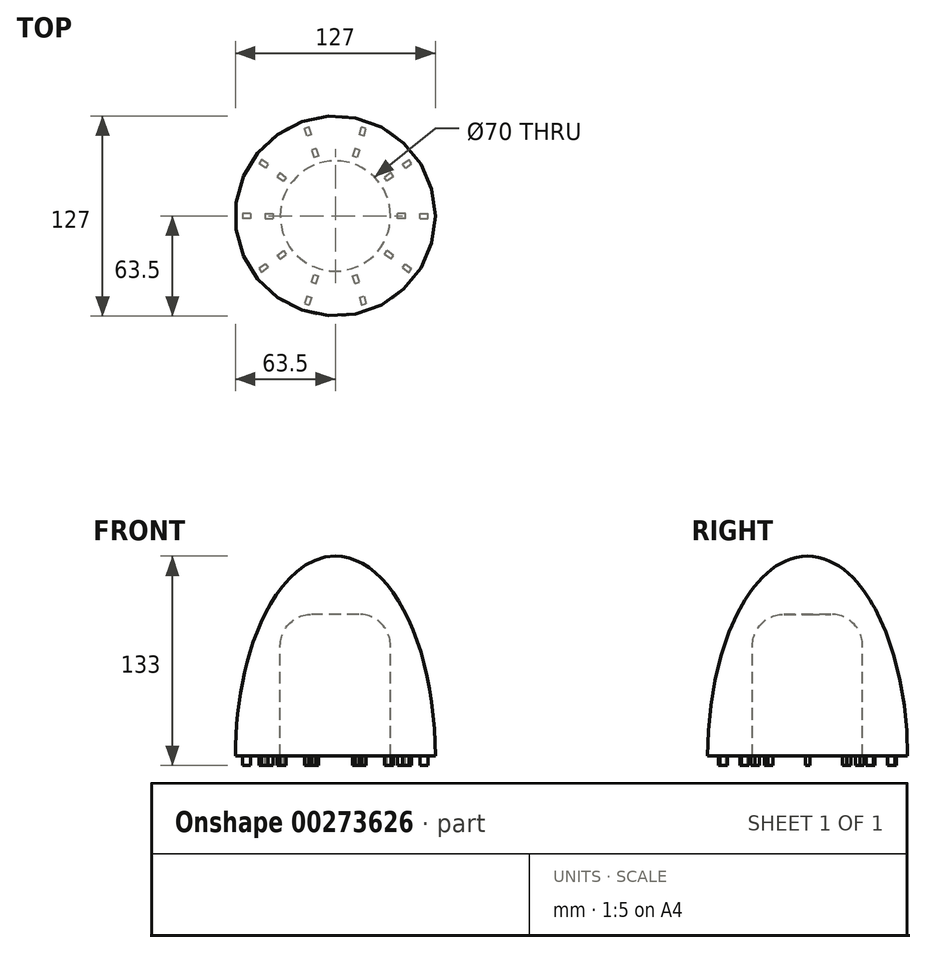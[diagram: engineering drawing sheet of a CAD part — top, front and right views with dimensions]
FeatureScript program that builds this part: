
annotation { "Feature Type Name" : "Feature", "Feature Type Description" : "" }
export const myFeature = defineFeature(function(context is Context, id is Id, definition is map)
    precondition{}
    {
        {
            var Q0;
            Q0=qCreatedBy(makeId("Front.planeOp"),FACE);
            var sketch = newSketch(context, id + "F0", { "sketchPlane" : qUnion([Q0])});
            skEllipticalArc(sketch, "E0", {});
            skLineSegment(sketch, "E1", {"start": v(0, 0) * mm, "end": v(0, 127) * mm});
            skLineSegment(sketch, "E2", {"start": v(0, 0) * mm, "end": v(63.5, 0) * mm});
            const initialGuessF0  = {"E0": [0, 0, 1, 0, 0.0635, 0.127, 6.283185307179586, 1.5707963267948966]};
            skSetInitialGuess(sketch, initialGuessF0);
            skSolve(sketch);
        }
        {
            var Q0;
            Q0=makeQuery(id+"F0.imprint","IMPRINT",FACE,{"disambiguationData":[TD([[makeQuery(id+"F0.imprint","IMPRINT",EDGE,{"derivedFrom":sQuery(id+"F0.wireOp",EDGE,"E0")}),1.0]])]});
            var Q1;
            Q1=sQuery(id+"F0.wireOp",EDGE,"E1");
            revolve(context, id + "F1", {"entities" : qUnion([Q0]), "axis" : qUnion([Q1]), "revolveType" : RevolveType.FULL});
        }
        {
            var Q0;
            Q0=qCreatedBy(makeId("Front.planeOp"),FACE);
            var sketch = newSketch(context, id + "F2", { "sketchPlane" : qUnion([Q0])});
            skLineSegment(sketch, "E3.bottom", {"start": v(15, 90) * mm, "end": v(0, 90) * mm});
            skLineSegment(sketch, "E3.left", {"start": v(35, 70) * mm, "end": v(35, 0) * mm});
            skPoint(sketch, "E3.middle", {"position": v(0, 0) * mm});
            skLineSegment(sketch, "E4", {"start": v(0, 0) * mm, "end": v(0, 90) * mm});
            skLineSegment(sketch, "E5", {"start": v(0, 0) * mm, "end": v(35, 0) * mm});
            skPoint(sketch, "E6.visualSharp", {"position": v(35, 90) * mm});
            skArc(sketch, "E6.filletArc", {"start": v(35, 70) * mm, "mid": v(29.14, 84.14) * mm, "end": v(15, 90) * mm});
            skSolve(sketch);
        }
        {
            var Q0;
            Q0 = qSketchRegion(id + "F2", true);
            var Q1;
            Q1=sQuery(id+"F2.wireOp",EDGE,"E4");
            revolve(context, id + "F3", {"operationType" : NewBodyOperationType.REMOVE, "entities" : qUnion([Q0]), "axis" : qUnion([Q1]), "revolveType" : RevolveType.FULL, "oppositeDirection" : true});
        }
        {
            var Q0;
            Q0=makeQuery(id+"F1.opRevolve","SWEPT_FACE",FACE,{"disambiguationData":[OSD([sQuery(id+"F0.wireOp",EDGE,"E2")])]});
            var sketch = newSketch(context, id + "F4", { "sketchPlane" : qUnion([Q0])});
            skPoint(sketch, "E7.endSnap0", {"position": v(-49.25, 0) * mm});
            skLineSegment(sketch, "E8.bottom", {"start": v(-53.88, -1.5) * mm, "end": v(-58.88, -1.5) * mm});
            skLineSegment(sketch, "E8.top", {"start": v(-53.88, 1.5) * mm, "end": v(-58.88, 1.5) * mm});
            skLineSegment(sketch, "E8.left", {"start": v(-53.88, -1.5) * mm, "end": v(-53.88, 1.5) * mm});
            skLineSegment(sketch, "E8.right", {"start": v(-58.88, -1.5) * mm, "end": v(-58.88, 1.5) * mm});
            skPoint(sketch, "E8.middle", {"position": v(-56.38, 0) * mm});
            skLineSegment(sketch, "E9.bottom", {"start": v(-44.63, -1.5) * mm, "end": v(-39.63, -1.5) * mm});
            skLineSegment(sketch, "E9.top", {"start": v(-44.63, 1.5) * mm, "end": v(-39.63, 1.5) * mm});
            skLineSegment(sketch, "E9.left", {"start": v(-44.63, -1.5) * mm, "end": v(-44.63, 1.5) * mm});
            skLineSegment(sketch, "E9.right", {"start": v(-39.63, -1.5) * mm, "end": v(-39.63, 1.5) * mm});
            skPoint(sketch, "E9.middle", {"position": v(-42.12, 0) * mm});
            skPoint(sketch, "E10.1.0", {"position": v(-45.6, -33.14) * mm});
            skLineSegment(sketch, "E10.1.1", {"start": v(-42.7, -32.88) * mm, "end": v(-44.47, -30.45) * mm});
            skLineSegment(sketch, "E10.1.2", {"start": v(-42.7, -32.88) * mm, "end": v(-46.75, -35.82) * mm});
            skLineSegment(sketch, "E10.1.3", {"start": v(-31.18, -24.5) * mm, "end": v(-32.94, -22.08) * mm});
            skLineSegment(sketch, "E10.1.4", {"start": v(-35.22, -27.44) * mm, "end": v(-36.98, -25.02) * mm});
            skLineSegment(sketch, "E10.1.5", {"start": v(-44.47, -30.45) * mm, "end": v(-48.51, -33.4) * mm});
            skLineSegment(sketch, "E10.1.6", {"start": v(-46.75, -35.82) * mm, "end": v(-48.51, -33.4) * mm});
            skLineSegment(sketch, "E10.1.7", {"start": v(-35.22, -27.44) * mm, "end": v(-31.18, -24.5) * mm});
            skLineSegment(sketch, "E10.1.8", {"start": v(-36.98, -25.02) * mm, "end": v(-32.94, -22.08) * mm});
            skPoint(sketch, "E10.1.9", {"position": v(-34.08, -24.76) * mm});
            skPoint(sketch, "E10.2.0", {"position": v(-17.42, -53.62) * mm});
            skLineSegment(sketch, "E10.2.1", {"start": v(-15.22, -51.7) * mm, "end": v(-18.07, -50.77) * mm});
            skLineSegment(sketch, "E10.2.2", {"start": v(-15.22, -51.7) * mm, "end": v(-16.77, -56.46) * mm});
            skLineSegment(sketch, "E10.2.3", {"start": v(-10.82, -38.15) * mm, "end": v(-13.67, -37.22) * mm});
            skLineSegment(sketch, "E10.2.4", {"start": v(-12.36, -42.9) * mm, "end": v(-15.22, -41.98) * mm});
            skLineSegment(sketch, "E10.2.5", {"start": v(-18.07, -50.77) * mm, "end": v(-19.62, -55.53) * mm});
            skLineSegment(sketch, "E10.2.6", {"start": v(-16.77, -56.46) * mm, "end": v(-19.62, -55.53) * mm});
            skLineSegment(sketch, "E10.2.7", {"start": v(-12.36, -42.9) * mm, "end": v(-10.82, -38.15) * mm});
            skLineSegment(sketch, "E10.2.8", {"start": v(-15.22, -41.98) * mm, "end": v(-13.67, -37.22) * mm});
            skPoint(sketch, "E10.2.9", {"position": v(-13.02, -40.06) * mm});
            skPoint(sketch, "E10.3.0", {"position": v(17.42, -53.62) * mm});
            skLineSegment(sketch, "E10.3.1", {"start": v(18.07, -50.77) * mm, "end": v(15.22, -51.7) * mm});
            skLineSegment(sketch, "E10.3.2", {"start": v(18.07, -50.77) * mm, "end": v(19.62, -55.53) * mm});
            skLineSegment(sketch, "E10.3.3", {"start": v(13.67, -37.22) * mm, "end": v(10.82, -38.15) * mm});
            skLineSegment(sketch, "E10.3.4", {"start": v(15.22, -41.98) * mm, "end": v(12.36, -42.9) * mm});
            skLineSegment(sketch, "E10.3.5", {"start": v(15.22, -51.7) * mm, "end": v(16.77, -56.46) * mm});
            skLineSegment(sketch, "E10.3.6", {"start": v(19.62, -55.53) * mm, "end": v(16.77, -56.46) * mm});
            skLineSegment(sketch, "E10.3.7", {"start": v(15.22, -41.98) * mm, "end": v(13.67, -37.22) * mm});
            skLineSegment(sketch, "E10.3.8", {"start": v(12.36, -42.9) * mm, "end": v(10.82, -38.15) * mm});
            skPoint(sketch, "E10.3.9", {"position": v(13.02, -40.06) * mm});
            skPoint(sketch, "E10.4.0", {"position": v(45.6, -33.14) * mm});
            skLineSegment(sketch, "E10.4.1", {"start": v(44.47, -30.45) * mm, "end": v(42.7, -32.88) * mm});
            skLineSegment(sketch, "E10.4.2", {"start": v(44.47, -30.45) * mm, "end": v(48.51, -33.4) * mm});
            skLineSegment(sketch, "E10.4.3", {"start": v(32.94, -22.08) * mm, "end": v(31.18, -24.5) * mm});
            skLineSegment(sketch, "E10.4.4", {"start": v(36.98, -25.02) * mm, "end": v(35.22, -27.44) * mm});
            skLineSegment(sketch, "E10.4.5", {"start": v(42.7, -32.88) * mm, "end": v(46.75, -35.82) * mm});
            skLineSegment(sketch, "E10.4.6", {"start": v(48.51, -33.4) * mm, "end": v(46.75, -35.82) * mm});
            skLineSegment(sketch, "E10.4.7", {"start": v(36.98, -25.02) * mm, "end": v(32.94, -22.08) * mm});
            skLineSegment(sketch, "E10.4.8", {"start": v(35.22, -27.44) * mm, "end": v(31.18, -24.5) * mm});
            skPoint(sketch, "E10.4.9", {"position": v(34.08, -24.76) * mm});
            skPoint(sketch, "E10.5.0", {"position": v(56.38, 0) * mm});
            skLineSegment(sketch, "E10.5.1", {"start": v(53.88, 1.5) * mm, "end": v(53.88, -1.5) * mm});
            skLineSegment(sketch, "E10.5.2", {"start": v(53.88, 1.5) * mm, "end": v(58.88, 1.5) * mm});
            skLineSegment(sketch, "E10.5.3", {"start": v(39.63, 1.5) * mm, "end": v(39.63, -1.5) * mm});
            skLineSegment(sketch, "E10.5.4", {"start": v(44.63, 1.5) * mm, "end": v(44.63, -1.5) * mm});
            skLineSegment(sketch, "E10.5.5", {"start": v(53.88, -1.5) * mm, "end": v(58.88, -1.5) * mm});
            skLineSegment(sketch, "E10.5.6", {"start": v(58.88, 1.5) * mm, "end": v(58.88, -1.5) * mm});
            skLineSegment(sketch, "E10.5.7", {"start": v(44.63, 1.5) * mm, "end": v(39.63, 1.5) * mm});
            skLineSegment(sketch, "E10.5.8", {"start": v(44.63, -1.5) * mm, "end": v(39.63, -1.5) * mm});
            skPoint(sketch, "E10.5.9", {"position": v(42.12, 0) * mm});
            skPoint(sketch, "E10.6.0", {"position": v(45.6, 33.14) * mm});
            skLineSegment(sketch, "E10.6.1", {"start": v(42.7, 32.88) * mm, "end": v(44.47, 30.45) * mm});
            skLineSegment(sketch, "E10.6.2", {"start": v(42.7, 32.88) * mm, "end": v(46.75, 35.82) * mm});
            skLineSegment(sketch, "E10.6.3", {"start": v(31.18, 24.5) * mm, "end": v(32.94, 22.08) * mm});
            skLineSegment(sketch, "E10.6.4", {"start": v(35.22, 27.44) * mm, "end": v(36.98, 25.02) * mm});
            skLineSegment(sketch, "E10.6.5", {"start": v(44.47, 30.45) * mm, "end": v(48.51, 33.4) * mm});
            skLineSegment(sketch, "E10.6.6", {"start": v(46.75, 35.82) * mm, "end": v(48.51, 33.4) * mm});
            skLineSegment(sketch, "E10.6.7", {"start": v(35.22, 27.44) * mm, "end": v(31.18, 24.5) * mm});
            skLineSegment(sketch, "E10.6.8", {"start": v(36.98, 25.02) * mm, "end": v(32.94, 22.08) * mm});
            skPoint(sketch, "E10.6.9", {"position": v(34.08, 24.76) * mm});
            skPoint(sketch, "E10.7.0", {"position": v(17.42, 53.62) * mm});
            skLineSegment(sketch, "E10.7.1", {"start": v(15.22, 51.7) * mm, "end": v(18.07, 50.77) * mm});
            skLineSegment(sketch, "E10.7.2", {"start": v(15.22, 51.7) * mm, "end": v(16.77, 56.46) * mm});
            skLineSegment(sketch, "E10.7.3", {"start": v(10.82, 38.15) * mm, "end": v(13.67, 37.22) * mm});
            skLineSegment(sketch, "E10.7.4", {"start": v(12.36, 42.9) * mm, "end": v(15.22, 41.98) * mm});
            skLineSegment(sketch, "E10.7.5", {"start": v(18.07, 50.77) * mm, "end": v(19.62, 55.53) * mm});
            skLineSegment(sketch, "E10.7.6", {"start": v(16.77, 56.46) * mm, "end": v(19.62, 55.53) * mm});
            skLineSegment(sketch, "E10.7.7", {"start": v(12.36, 42.9) * mm, "end": v(10.82, 38.15) * mm});
            skLineSegment(sketch, "E10.7.8", {"start": v(15.22, 41.98) * mm, "end": v(13.67, 37.22) * mm});
            skPoint(sketch, "E10.7.9", {"position": v(13.02, 40.06) * mm});
            skPoint(sketch, "E10.8.0", {"position": v(-17.42, 53.62) * mm});
            skLineSegment(sketch, "E10.8.1", {"start": v(-18.07, 50.77) * mm, "end": v(-15.22, 51.7) * mm});
            skLineSegment(sketch, "E10.8.2", {"start": v(-18.07, 50.77) * mm, "end": v(-19.62, 55.53) * mm});
            skLineSegment(sketch, "E10.8.3", {"start": v(-13.67, 37.22) * mm, "end": v(-10.82, 38.15) * mm});
            skLineSegment(sketch, "E10.8.4", {"start": v(-15.22, 41.98) * mm, "end": v(-12.36, 42.9) * mm});
            skLineSegment(sketch, "E10.8.5", {"start": v(-15.22, 51.7) * mm, "end": v(-16.77, 56.46) * mm});
            skLineSegment(sketch, "E10.8.6", {"start": v(-19.62, 55.53) * mm, "end": v(-16.77, 56.46) * mm});
            skLineSegment(sketch, "E10.8.7", {"start": v(-15.22, 41.98) * mm, "end": v(-13.67, 37.22) * mm});
            skLineSegment(sketch, "E10.8.8", {"start": v(-12.36, 42.9) * mm, "end": v(-10.82, 38.15) * mm});
            skPoint(sketch, "E10.8.9", {"position": v(-13.02, 40.06) * mm});
            skPoint(sketch, "E10.9.0", {"position": v(-45.6, 33.14) * mm});
            skLineSegment(sketch, "E10.9.1", {"start": v(-44.47, 30.45) * mm, "end": v(-42.7, 32.88) * mm});
            skLineSegment(sketch, "E10.9.2", {"start": v(-44.47, 30.45) * mm, "end": v(-48.51, 33.4) * mm});
            skLineSegment(sketch, "E10.9.3", {"start": v(-32.94, 22.08) * mm, "end": v(-31.18, 24.5) * mm});
            skLineSegment(sketch, "E10.9.4", {"start": v(-36.98, 25.02) * mm, "end": v(-35.22, 27.44) * mm});
            skLineSegment(sketch, "E10.9.5", {"start": v(-42.7, 32.88) * mm, "end": v(-46.75, 35.82) * mm});
            skLineSegment(sketch, "E10.9.6", {"start": v(-48.51, 33.4) * mm, "end": v(-46.75, 35.82) * mm});
            skLineSegment(sketch, "E10.9.7", {"start": v(-36.98, 25.02) * mm, "end": v(-32.94, 22.08) * mm});
            skLineSegment(sketch, "E10.9.8", {"start": v(-35.22, 27.44) * mm, "end": v(-31.18, 24.5) * mm});
            skPoint(sketch, "E10.9.9", {"position": v(-34.08, 24.76) * mm});
            skPoint(sketch, "E10.center", {"position": v(0, 0) * mm});
            skSolve(sketch);
        }
        {
            var Q0;
            Q0 = qSketchRegion(id + "F4", true);
            extrude(context, id + "F5", {"entities" : qUnion([Q0]), "operationType" : NewBodyOperationType.ADD, "depth" : 6 * mm});
        }
    });
